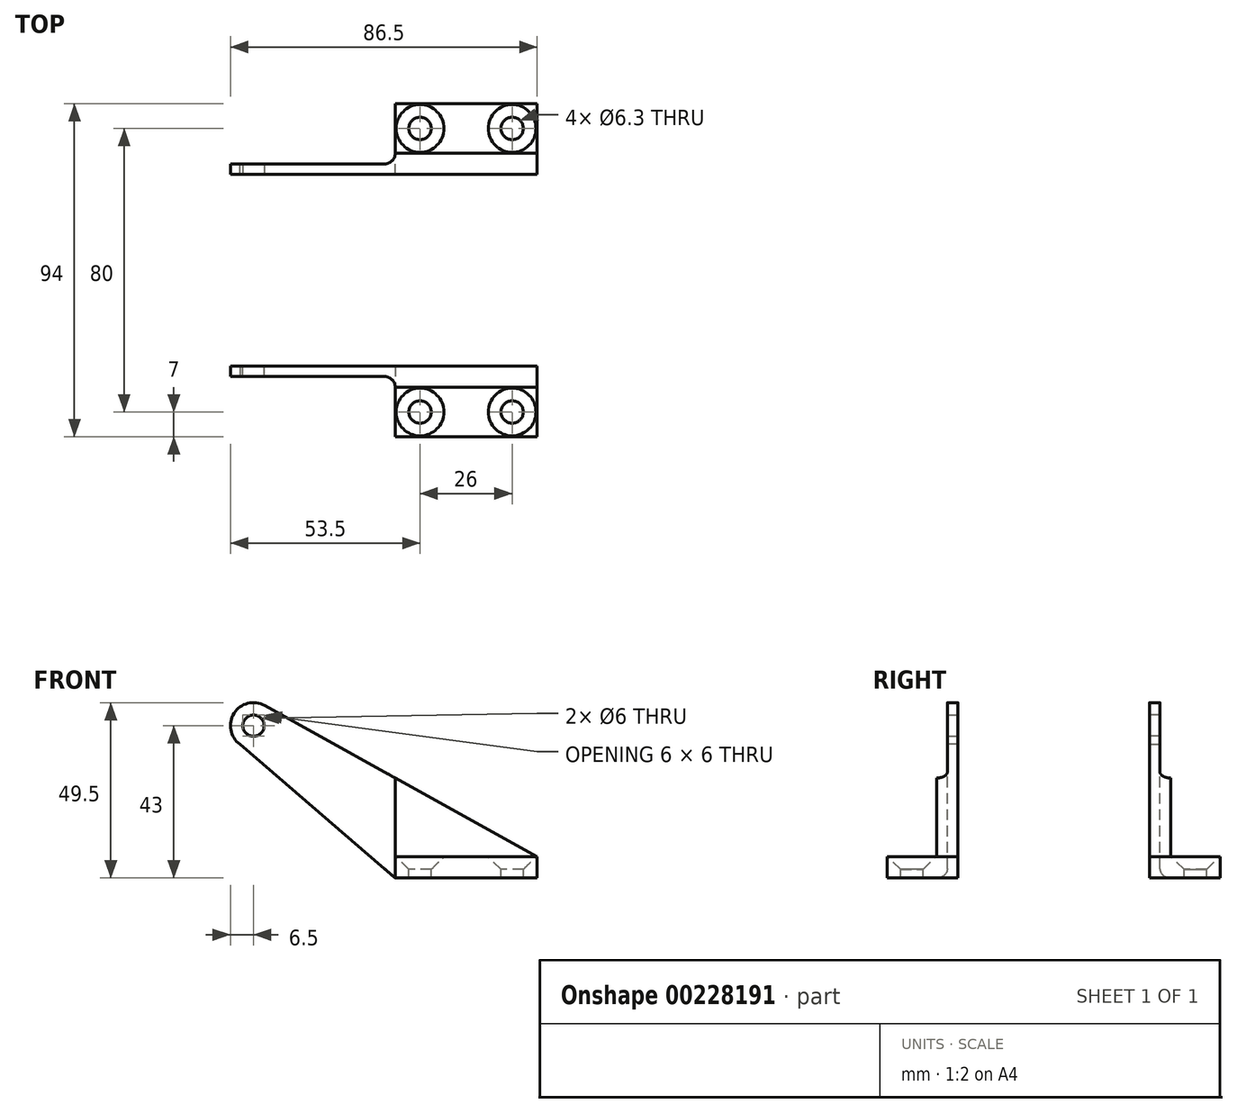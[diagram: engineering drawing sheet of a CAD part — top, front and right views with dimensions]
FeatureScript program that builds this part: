
annotation { "Feature Type Name" : "Feature", "Feature Type Description" : "" }
export const myFeature = defineFeature(function(context is Context, id is Id, definition is map)
    precondition{}
    {
        {
            var Q0;
            Q0=qCreatedBy(makeId("Right.planeOp"),FACE);
            var sketch = newSketch(context, id + "F0", { "sketchPlane" : qUnion([Q0])});
            skLineSegment(sketch, "E0", {"start": v(0, 0) * mm, "end": v(0, 50) * mm});
            skLineSegment(sketch, "E1", {"start": v(0, 50) * mm, "end": v(6, 50) * mm});
            skLineSegment(sketch, "E2", {"start": v(0, 0) * mm, "end": v(50, 0) * mm});
            skLineSegment(sketch, "E3", {"start": v(50, 0) * mm, "end": v(50, 6) * mm});
            skLineSegment(sketch, "E4", {"start": v(50, 6) * mm, "end": v(6, 6) * mm});
            skLineSegment(sketch, "E5", {"start": v(6, 6) * mm, "end": v(6, 50) * mm});
            skSolve(sketch);
        }
        {
            var Q0;
            Q0=makeQuery(id+"F0.imprint","IMPRINT",FACE,{"disambiguationData":[TD([[makeQuery(id+"F0.imprint","IMPRINT",EDGE,{"derivedFrom":sQuery(id+"F0.wireOp",EDGE,"E0")}),-1.0]])]});
            extrude(context, id + "F1", {"entities" : qUnion([Q0]), "oppositeDirection" : true, "depth" : 100 * mm});
        }
        {
            var Q0;
            Q0=makeQuery(id+"F1.opExtrude","SWEPT_FACE",FACE,{"disambiguationData":[OSD([sQuery(id+"F0.wireOp",EDGE,"E4")])]});
            var sketch = newSketch(context, id + "F2", { "sketchPlane" : qUnion([Q0])});
            skCircle(sketch, "E6", {"center": v(-7, 13) * mm, "radius": 2.5 * mm});
            skCircle(sketch, "E7", {"center": v(-33, 13) * mm, "radius": 2.5 * mm});
            skSolve(sketch);
        }
        {
            var Q0;
            Q0=makeQuery(id+"F1.opExtrude","SWEPT_FACE",FACE,{"disambiguationData":[OSD([sQuery(id+"F0.wireOp",EDGE,"E0")])]});
            var sketch = newSketch(context, id + "F3", { "sketchPlane" : qUnion([Q0])});
            skCircle(sketch, "E8", {"center": v(-80, 43) * mm, "radius": 3 * mm});
            skSolve(sketch);
        }
        {
            var Q0;
            Q0 = qSketchRegion(id + "F3", true);
            extrude(context, id + "F4", {"entities" : qUnion([Q0]), "operationType" : NewBodyOperationType.REMOVE, "oppositeDirection" : true, "depth" : 25 * mm});
        }
        {
            var Q0;
            Q0=makeQuery(id+"F1.opExtrude","SWEPT_FACE",FACE,{"disambiguationData":[OSD([sQuery(id+"F0.wireOp",EDGE,"E2")])]});
            var sketch = newSketch(context, id + "F5", { "sketchPlane" : qUnion([Q0])});
            skLineSegment(sketch, "E9", {"start": v(-40, -6) * mm, "end": v(-40, -20) * mm});
            skLineSegment(sketch, "E10", {"start": v(-40, -20) * mm, "end": v(0, -20) * mm});
            skLineSegment(sketch, "E11", {"start": v(-100, -6) * mm, "end": v(-100, -50) * mm});
            skLineSegment(sketch, "E12", {"start": v(-100, -50) * mm, "end": v(0, -50) * mm});
            skLineSegment(sketch, "E13", {"start": v(0, -50) * mm, "end": v(0, -20) * mm});
            skLineSegment(sketch, "E14", {"start": v(-40, -6) * mm, "end": v(-100, -6) * mm});
            skSolve(sketch);
        }
        {
            var Q0;
            Q0 = qSketchRegion(id + "F5", true);
            extrude(context, id + "F6", {"entities" : qUnion([Q0]), "operationType" : NewBodyOperationType.REMOVE, "oppositeDirection" : true, "depth" : 6 * mm});
        }
        {
            var Q0;
            Q0=makeQuery(id+"F1.opExtrude","SWEPT_FACE",FACE,{"disambiguationData":[OSD([sQuery(id+"F0.wireOp",EDGE,"E5")])]});
            var sketch = newSketch(context, id + "F7", { "sketchPlane" : qUnion([Q0])});
            skArc(sketch, "E15", {"start": v(83.81, 37.74) * mm, "mid": v(85.48, 46.5) * mm, "end": v(76.84, 48.68) * mm});
            skLineSegment(sketch, "E16", {"start": v(0, 6) * mm, "end": v(76.84, 48.68) * mm});
            skLineSegment(sketch, "E17", {"start": v(0, 6) * mm, "end": v(0, 50) * mm});
            skLineSegment(sketch, "E18", {"start": v(0, 50) * mm, "end": v(100, 50) * mm});
            skLineSegment(sketch, "E19", {"start": v(83.81, 37.74) * mm, "end": v(40, 0) * mm});
            skLineSegment(sketch, "E20", {"start": v(100, 50) * mm, "end": v(100, 0) * mm});
            skLineSegment(sketch, "E21", {"start": v(100, 0) * mm, "end": v(40, 0) * mm});
            skSolve(sketch);
        }
        {
            var Q0;
            Q0 = qSketchRegion(id + "F7", true);
            extrude(context, id + "F8", {"entities" : qUnion([Q0]), "operationType" : NewBodyOperationType.REMOVE, "oppositeDirection" : true, "depth" : 25 * mm});
        }
        {
            var Q0;
            Q0=makeQuery(id+"F6.boolean.opBoolean","MERGE",FACE,{"derivedFrom":[makeQuery(id+"F1.opExtrude","SWEPT_FACE",FACE,{"disambiguationData":[OSD([sQuery(id+"F0.wireOp",EDGE,"E5")])]}),makeQuery(id+"F6.opExtrude","SWEPT_FACE",FACE,{"disambiguationData":[OSD([sQuery(id+"F5.wireOp",EDGE,"E14")])]})]});
            var sketch = newSketch(context, id + "F9", { "sketchPlane" : qUnion([Q0])});
            skLineSegment(sketch, "E22", {"start": v(40, 0) * mm, "end": v(40, 28.22) * mm});
            skLineSegment(sketch, "E23", {"start": v(40, 28.22) * mm, "end": v(83.24, 63.8) * mm});
            skLineSegment(sketch, "E24", {"start": v(83.24, 63.8) * mm, "end": v(106.4, 23.9) * mm});
            skLineSegment(sketch, "E25", {"start": v(106.4, 23.9) * mm, "end": v(40, 0) * mm});
            skSolve(sketch);
        }
        {
            var Q0;
            Q0 = qSketchRegion(id + "F9", true);
            extrude(context, id + "F10", {"entities" : qUnion([Q0]), "operationType" : NewBodyOperationType.REMOVE, "oppositeDirection" : true, "depth" : 3 * mm});
        }
        {
            var Q0;
            Q0=makeQuery(id+"F10.boolean.opBoolean","COPY",EDGE,{"derivedFrom":makeQuery(id+"F10.opExtrude","CAP_EDGE",EDGE,{"disambiguationData":[OSD([sQuery(id+"F9.wireOp",EDGE,"E22")])],"isStart":false})});
            fillet(context, id + "F11", {"entities" : qUnion([Q0]), "radius" : 3 * mm, "tangentPropagation" : true, "allowEdgeOverflow" : false});
        }
        {
            var Q0;
            Q0=sQuery(id+"F2.wireOp",VERTEX,"E6.center");
            var Q1;
            Q1=sQuery(id+"F2.wireOp",VERTEX,"E7.center");
            var Q2;
            Q2=makeQuery(id+"F1.opExtrude","SWEPT_BODY",BODY,{"disambiguationData":[OSD([sQuery(id+"F0.wireOp",EDGE,"E0"),sQuery(id+"F0.wireOp",EDGE,"E1"),sQuery(id+"F0.wireOp",EDGE,"E2"),sQuery(id+"F0.wireOp",EDGE,"E3"),sQuery(id+"F0.wireOp",EDGE,"E4"),sQuery(id+"F0.wireOp",EDGE,"E5")])]});
            hole(context, id + "F12", {"style" : HoleStyle.C_SINK, "endStyle" : HoleEndStyle.THROUGH, "standardTappedOrClearance" : lookupTablePath({ "standard" : "ISO", "fit" : "Close", "size" : "M6", "type" : "Clearance" }), "standardBlindInLast" : lookupTablePath({ "fit" : "Close", "standard" : "ISO", "size" : "M6", "type" : "Clearance" }), "holeDiameter" : 6.3 * mm, "cSinkDiameter" : 13.44 * mm, "cSinkAngle" : 90 * degree, "locations" : qUnion([Q0, Q1]), "scope" : qUnion([Q2]), "isTappedThrough" : true});
        }
        {
            var Q0;
            Q0=makeQuery(id+"F1.opExtrude","SWEPT_FACE",FACE,{"disambiguationData":[OSD([sQuery(id+"F0.wireOp",EDGE,"E0")])]});
            cPlane(context, id + "F13", {"entities" : qUnion([Q0]), "cplaneType" : CPlaneType.OFFSET, "offset" : 27 * mm, "width" : 150 * mm, "height" : 150 * mm});
        }
        {
            var Q0;
            Q0=makeQuery(id+"F1.opExtrude","SWEPT_BODY",BODY,{"disambiguationData":[OSD([sQuery(id+"F0.wireOp",EDGE,"E0"),sQuery(id+"F0.wireOp",EDGE,"E1"),sQuery(id+"F0.wireOp",EDGE,"E2"),sQuery(id+"F0.wireOp",EDGE,"E3"),sQuery(id+"F0.wireOp",EDGE,"E4"),sQuery(id+"F0.wireOp",EDGE,"E5")])]});
            var Q1;
            Q1=qCreatedBy(id+"F13.planeOp",FACE);
            mirror(context, id + "F14", {"entities" : qUnion([Q0]), "mirrorPlane" : qUnion([Q1])});
        }
    });
